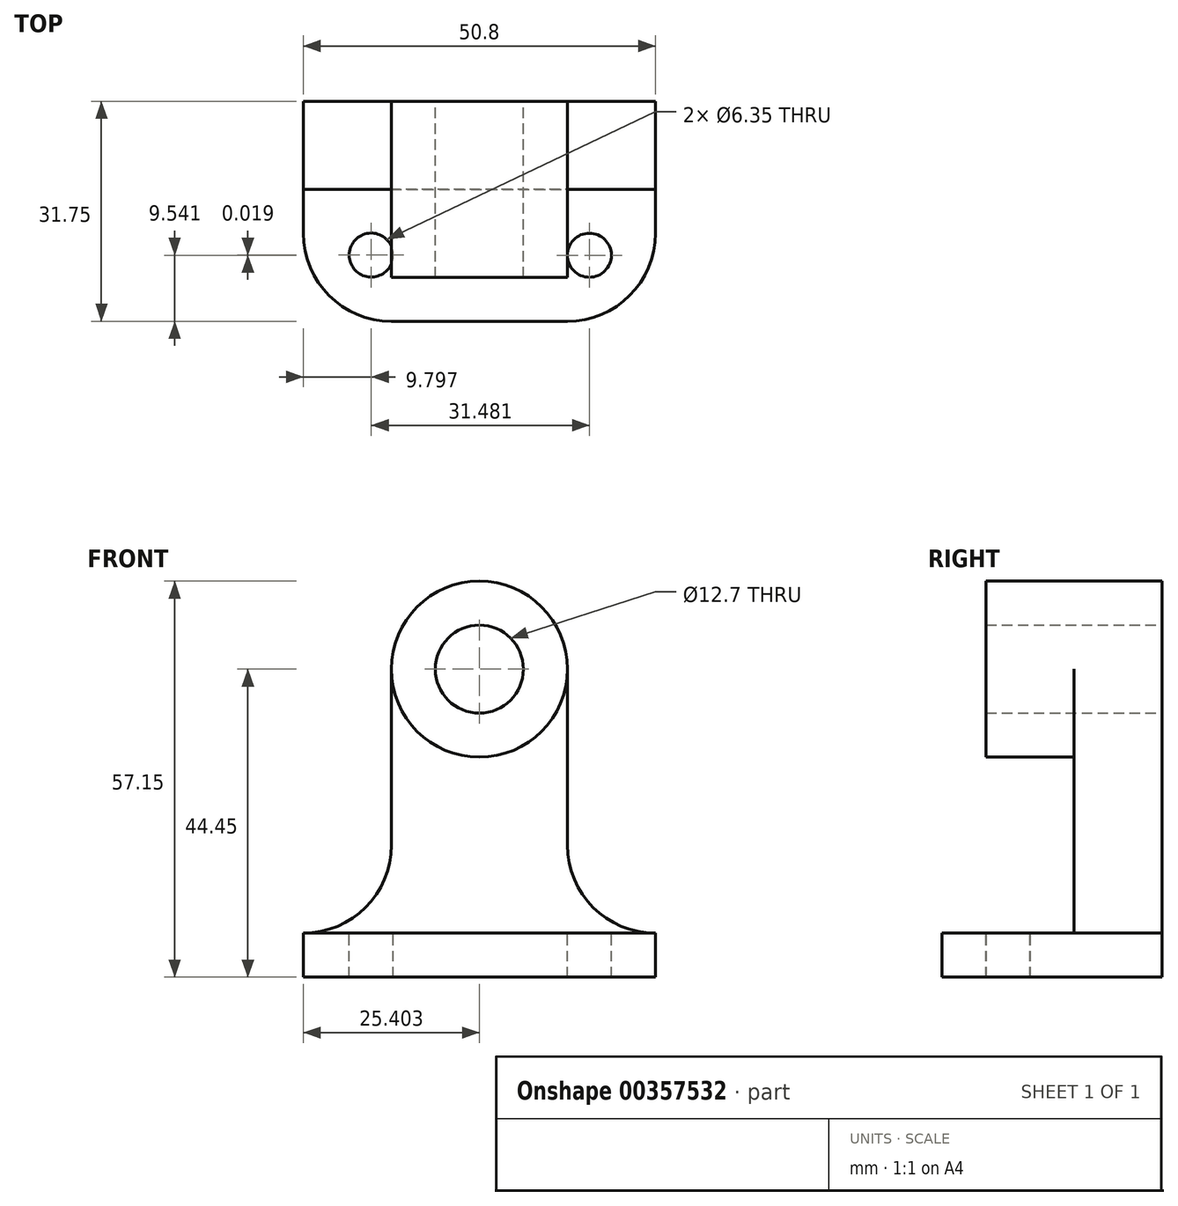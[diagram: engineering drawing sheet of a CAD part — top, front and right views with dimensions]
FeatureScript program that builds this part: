
annotation { "Feature Type Name" : "Feature", "Feature Type Description" : "" }
export const myFeature = defineFeature(function(context is Context, id is Id, definition is map)
    precondition{}
    {
        {
            var Q0;
            Q0=qCreatedBy(makeId("Front.planeOp"),FACE);
            var sketch = newSketch(context, id + "F0", { "sketchPlane" : qUnion([Q0])});
            skLineSegment(sketch, "E0", {"start": v(-55.35, 50.8) * mm, "end": v(-55.35, -6.35) * mm});
            skLineSegment(sketch, "E1", {"start": v(-55.35, -6.35) * mm, "end": v(-4.55, -6.35) * mm});
            skLineSegment(sketch, "E2", {"start": v(-4.55, -6.35) * mm, "end": v(-4.55, 50.8) * mm});
            skLineSegment(sketch, "E3", {"start": v(-4.55, 50.8) * mm, "end": v(-55.35, 50.8) * mm});
            skLineSegment(sketch, "E4", {"start": v(-55.35, -6.35) * mm, "end": v(-55.35, 0) * mm});
            skLineSegment(sketch, "E5", {"start": v(-55.35, 0) * mm, "end": v(-55.35, 0) * mm});
            skLineSegment(sketch, "E6", {"start": v(-55.35, 50.8) * mm, "end": v(-29.95, 50.8) * mm});
            skLineSegment(sketch, "E7", {"start": v(-29.95, 50.8) * mm, "end": v(-29.95, 38.1) * mm});
            skCircle(sketch, "E8", {"center": v(-29.95, 38.1) * mm, "radius": 12.7 * mm});
            skLineSegment(sketch, "E9", {"start": v(-29.95, 38.1) * mm, "end": v(-29.95, 44.45) * mm});
            skCircle(sketch, "E10", {"center": v(-29.95, 38.1) * mm, "radius": 6.35 * mm});
            skLineSegment(sketch, "E11", {"start": v(-55.35, 50.8) * mm, "end": v(-55.35, 0) * mm});
            skLineSegment(sketch, "E12", {"start": v(-4.55, 0) * mm, "end": v(-4.55, 0) * mm});
            skLineSegment(sketch, "E13", {"start": v(-4.55, 0) * mm, "end": v(-4.55, 50.8) * mm});
            skLineSegment(sketch, "E14", {"start": v(-55.35, 50.8) * mm, "end": v(-4.55, 50.8) * mm});
            skLineSegment(sketch, "E15", {"start": v(-4.55, 50.8) * mm, "end": v(-17.25, 50.8) * mm});
            skLineSegment(sketch, "E16", {"start": v(-17.25, 50.8) * mm, "end": v(-17.25, 38.1) * mm});
            skLineSegment(sketch, "E17", {"start": v(-17.25, 38.1) * mm, "end": v(-17.25, 12.7) * mm});
            skLineSegment(sketch, "E18", {"start": v(-55.35, 50.8) * mm, "end": v(-42.65, 50.8) * mm});
            skLineSegment(sketch, "E19", {"start": v(-42.65, 50.8) * mm, "end": v(-42.65, 38.1) * mm});
            skLineSegment(sketch, "E20", {"start": v(-42.65, 38.1) * mm, "end": v(-42.65, 12.7) * mm});
            skLineSegment(sketch, "E21", {"start": v(-42.65, 12.7) * mm, "end": v(-55.35, 12.7) * mm});
            skLineSegment(sketch, "E22", {"start": v(-17.25, 12.7) * mm, "end": v(-4.55, 12.7) * mm});
            skLineSegment(sketch, "E23", {"start": v(-17.25, 12.7) * mm, "end": v(-17.25, 12.7) * mm});
            skLineSegment(sketch, "E24", {"start": v(-17.25, 0) * mm, "end": v(-4.55, 0) * mm});
            skLineSegment(sketch, "E25", {"start": v(-4.55, 0) * mm, "end": v(-17.25, 0) * mm});
            skPoint(sketch, "E26.newPointA", {"position": v(-17.25, 0) * mm});
            skArc(sketch, "E26.filletArc", {"start": v(-17.25, 12.7) * mm, "mid": v(-13.53, 3.72) * mm, "end": v(-4.55, 0) * mm});
            skLineSegment(sketch, "E27", {"start": v(-42.65, 12.7) * mm, "end": v(-42.65, 12.7) * mm});
            skLineSegment(sketch, "E28", {"start": v(-42.65, 0) * mm, "end": v(-55.35, 0) * mm});
            skPoint(sketch, "E29.newPointA", {"position": v(-42.65, 0) * mm});
            skArc(sketch, "E29.filletArc", {"start": v(-55.35, 0) * mm, "mid": v(-46.37, 3.72) * mm, "end": v(-42.65, 12.7) * mm});
            skLineSegment(sketch, "E30", {"start": v(-55.35, 0) * mm, "end": v(-4.55, 0) * mm});
            skSolve(sketch);
        }
        {
            var Q0;
            {var subQ0=sQuery(id+"F0.wireOp",EDGE,"E1");Q0=makeQuery(id+"F0.imprint","IMPRINT",FACE,{"disambiguationData":[TD([[makeQuery(id+"F0.imprint","IMPRINT",EDGE,{"derivedFrom":subQ0}),1.0]])]});}
            extrude(context, id + "F1", {"entities" : qUnion([Q0]), "depth" : 31.75 * mm});
        }
        {
            var Q0;
            Q0=makeQuery(id+"F0.imprint","IMPRINT",FACE,{"disambiguationData":[TD([[makeQuery(id+"F0.imprint","IMPRINT",EDGE,{"derivedFrom":sQuery(id+"F0.wireOp",EDGE,"E8")}),1.0]])]});
            extrude(context, id + "F2", {"entities" : qUnion([Q0]), "operationType" : NewBodyOperationType.ADD, "depth" : 25.4 * mm});
        }
        {
            var Q0;
            {var subQ2=sQuery(id+"F0.wireOp",EDGE,"E17");Q0=makeQuery(id+"F0.imprint","IMPRINT",FACE,{"disambiguationData":[TD([[makeQuery(id+"F0.imprint","IMPRINT",EDGE,{"derivedFrom":subQ2}),-1.0]])]});}
            extrude(context, id + "F3", {"entities" : qUnion([Q0]), "operationType" : NewBodyOperationType.ADD, "depth" : 12.7 * mm});
        }
        {
            var Q0;
            Q0=makeQuery(id+"F1.opExtrude","SWEPT_FACE",FACE,{"disambiguationData":[OSD([sQuery(id+"F0.wireOp",EDGE,"E30")])]});
            var sketch = newSketch(context, id + "F4", { "sketchPlane" : qUnion([Q0])});
            skLineSegment(sketch, "E31", {"start": v(-4.55, 0) * mm, "end": v(-4.55, -19.05) * mm});
            skLineSegment(sketch, "E32", {"start": v(-17.25, -31.75) * mm, "end": v(-42.65, -31.75) * mm});
            skLineSegment(sketch, "E33", {"start": v(-55.35, -19.05) * mm, "end": v(-55.35, 0) * mm});
            skPoint(sketch, "E34.visualSharp", {"position": v(-4.55, -31.75) * mm});
            skArc(sketch, "E34.filletArc", {"start": v(-17.25, -31.75) * mm, "mid": v(-8.27, -28.03) * mm, "end": v(-4.55, -19.05) * mm});
            skPoint(sketch, "E35.visualSharp", {"position": v(-55.35, -31.75) * mm});
            skArc(sketch, "E35.filletArc", {"start": v(-55.35, -19.05) * mm, "mid": v(-51.63, -28.03) * mm, "end": v(-42.65, -31.75) * mm});
            skSolve(sketch);
        }
        {
            var Q0;
            {var subQ0=sQuery(id+"F4.wireOp",EDGE,"E35.filletArc");Q0=makeQuery(id+"F4.imprint","IMPRINT",FACE,{"disambiguationData":[TD([[makeQuery(id+"F4.imprint","IMPRINT",EDGE,{"derivedFrom":subQ0}),-1.0]])]});}
            var Q1;
            {var subQ0=sQuery(id+"F4.wireOp",EDGE,"E34.filletArc");Q1=makeQuery(id+"F4.imprint","IMPRINT",FACE,{"disambiguationData":[TD([[makeQuery(id+"F4.imprint","IMPRINT",EDGE,{"derivedFrom":subQ0}),-1.0]])]});}
            extrude(context, id + "F5", {"entities" : qUnion([Q0, Q1]), "operationType" : NewBodyOperationType.REMOVE, "oppositeDirection" : true, "depth" : 6.35 * mm});
        }
        {
            var Q0;
            Q0=makeQuery(id+"F1.opExtrude","SWEPT_FACE",FACE,{"disambiguationData":[OSD([sQuery(id+"F0.wireOp",EDGE,"E30")])]});
            var sketch = newSketch(context, id + "F6", { "sketchPlane" : qUnion([Q0])});
            skLineSegment(sketch, "E36", {"start": v(-17.25, 0) * mm, "end": v(-17.25, -12.7) * mm});
            skCircle(sketch, "E37", {"center": v(-14.07, -22.2) * mm, "radius": 3.18 * mm});
            skCircle(sketch, "E38", {"center": v(-45.55, -22.2) * mm, "radius": 3.17 * mm});
            skSolve(sketch);
        }
        {
            var Q0;
            Q0=makeQuery(id+"F6.imprint","IMPRINT",FACE,{"disambiguationData":[TD([[makeQuery(id+"F6.imprint","IMPRINT",EDGE,{"derivedFrom":sQuery(id+"F6.wireOp",EDGE,"E38")}),1.0]])]});
            var Q1;
            Q1=makeQuery(id+"F6.imprint","IMPRINT",FACE,{"disambiguationData":[TD([[makeQuery(id+"F6.imprint","IMPRINT",EDGE,{"derivedFrom":sQuery(id+"F6.wireOp",EDGE,"E37")}),1.0]])]});
            extrude(context, id + "F7", {"entities" : qUnion([Q0, Q1]), "operationType" : NewBodyOperationType.REMOVE, "oppositeDirection" : true, "depth" : 6.35 * mm});
        }
    });
